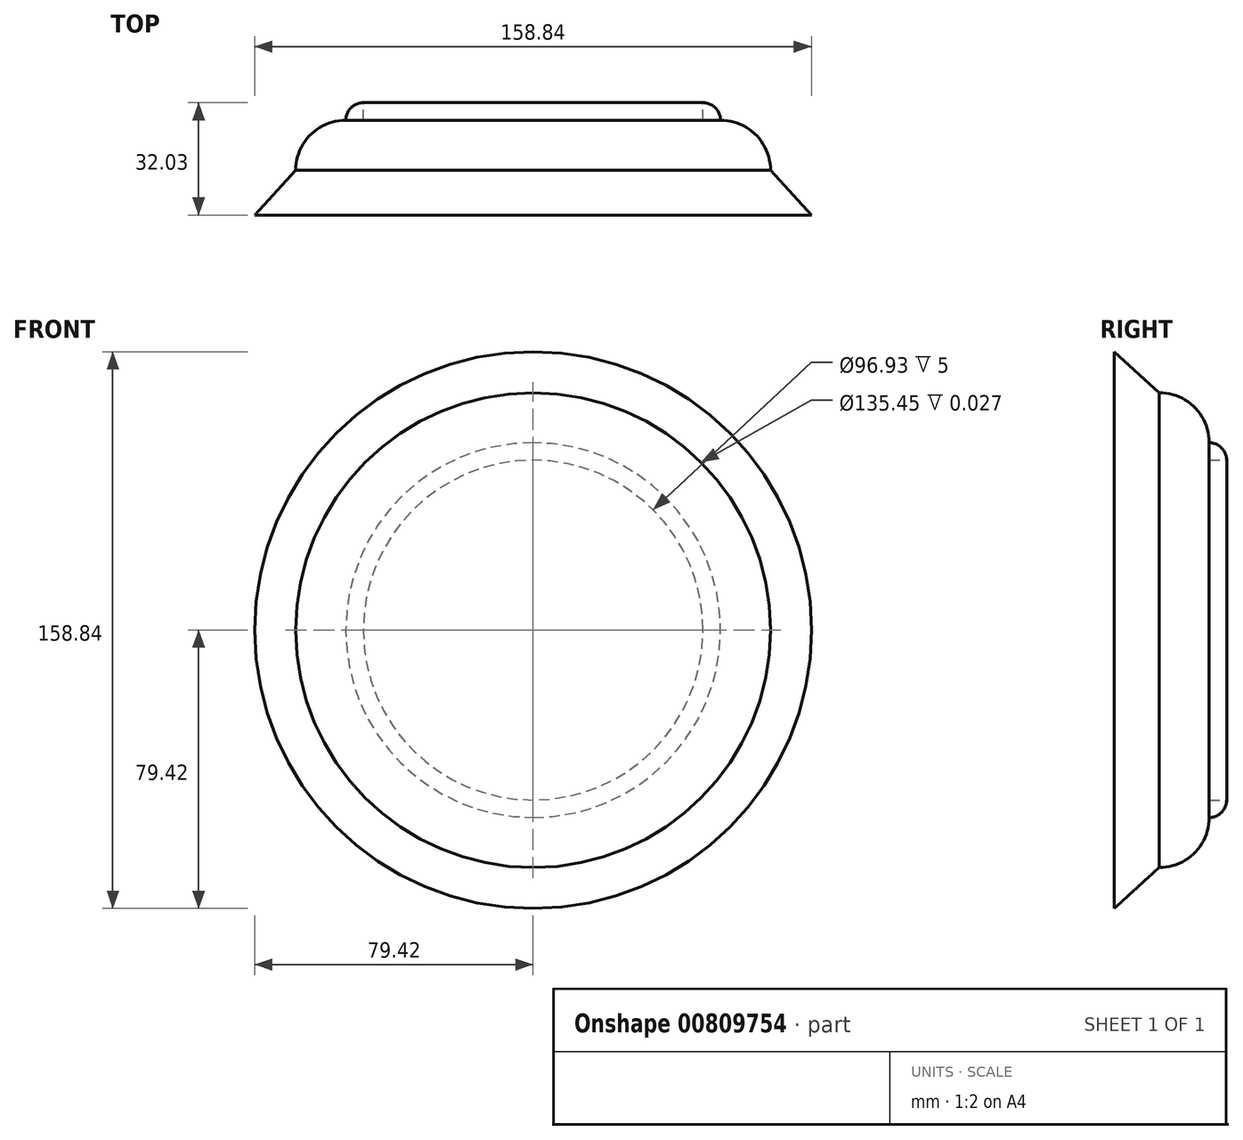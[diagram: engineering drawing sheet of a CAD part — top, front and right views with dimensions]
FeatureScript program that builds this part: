
annotation { "Feature Type Name" : "Feature", "Feature Type Description" : "" }
export const myFeature = defineFeature(function(context is Context, id is Id, definition is map)
    precondition{}
    {
        {
            var Q0;
            Q0=qCreatedBy(makeId("Front.planeOp"),FACE);
            var sketch = newSketch(context, id + "F0", { "sketchPlane" : qUnion([Q0])});
            skCircle(sketch, "E0", {"center": v(0, 0) * mm, "radius": 67.73 * mm});
            skSolve(sketch);
        }
        {
            var Q0;
            Q0=makeQuery(id+"F0.imprint","IMPRINT",FACE,{"disambiguationData":[TD([[makeQuery(id+"F0.imprint","IMPRINT",EDGE,{"derivedFrom":sQuery(id+"F0.wireOp",EDGE,"E0")}),1.0]])]});
            extrude(context, id + "F1", {"entities" : qUnion([Q0]), "depth" : 27 * mm, "offsetDistance" : 25 * mm});
        }
        {
            var Q0;
            Q0=makeQuery(id+"F1.opExtrude","CAP_FACE",FACE,{"disambiguationData":[OSD([sQuery(id+"F0.wireOp",EDGE,"E0")])],"isStart":true});
            var sketch = newSketch(context, id + "F2", { "sketchPlane" : qUnion([Q0])});
            skCircle(sketch, "E1", {"center": v(0, 0) * mm, "radius": 47.7 * mm});
            skSolve(sketch);
        }
        {
            var Q0;
            Q0=makeQuery(id+"F1.opExtrude","CAP_EDGE",EDGE,{"disambiguationData":[OSD([sQuery(id+"F0.wireOp",EDGE,"E0")])],"isStart":true});
            fillet(context, id + "F3", {"entities" : qUnion([Q0]), "radius" : 14.24 * mm, "tangentPropagation" : true, "allowEdgeOverflow" : false});
        }
        {
            var Q0;
            Q0=makeQuery(id+"F2.imprint","IMPRINT",FACE,{"disambiguationData":[TD([[makeQuery(id+"F2.imprint","IMPRINT",EDGE,{"derivedFrom":sQuery(id+"F2.wireOp",EDGE,"E1")}),1.0]])]});
            var sketch = newSketch(context, id + "F4", { "sketchPlane" : qUnion([Q0])});
            skCircle(sketch, "E2", {"center": v(0, 0) * mm, "radius": 53.46 * mm});
            skSolve(sketch);
        }
        {
            var Q0;
            Q0=makeQuery(id+"F4.imprint","IMPRINT",FACE,{"disambiguationData":[TD([[makeQuery(id+"F4.imprint","IMPRINT",EDGE,{"derivedFrom":sQuery(id+"F4.wireOp",EDGE,"E2")}),1.0]])]});
            extrude(context, id + "F5", {"entities" : qUnion([Q0]), "operationType" : NewBodyOperationType.ADD, "depth" : 5 * mm, "offsetDistance" : 25 * mm});
        }
        {
            var Q0;
            Q0=makeQuery(id+"F5.opExtrude","CAP_EDGE",EDGE,{"disambiguationData":[OSD([sQuery(id+"F4.wireOp",EDGE,"E2")])],"isStart":false});
            fillet(context, id + "F6", {"entities" : qUnion([Q0]), "radius" : 5 * mm, "tangentPropagation" : true, "allowEdgeOverflow" : false});
        }
        {
            var Q0;
            Q0=makeQuery(id+"F5.opExtrude","CAP_FACE",FACE,{"disambiguationData":[OSD([sQuery(id+"F2.wireOp",EDGE,"E1"),sQuery(id+"F4.wireOp",EDGE,"E2")])],"isStart":false});
            extrude(context, id + "F7", {"entities" : qUnion([Q0]), "operationType" : NewBodyOperationType.REMOVE, "oppositeDirection" : true, "depth" : 5 * mm, "offsetDistance" : 25 * mm});
        }
        {
            var Q0;
            Q0=qCreatedBy(makeId("Right.planeOp"),FACE);
            var sketch = newSketch(context, id + "F8", { "sketchPlane" : qUnion([Q0])});
            skLineSegment(sketch, "E3", {"start": v(-27.03, 0) * mm, "end": v(0, 0) * mm});
            skLineSegment(sketch, "E4", {"start": v(-27.03, 0) * mm, "end": v(-27.03, 79.42) * mm});
            skLineSegment(sketch, "E5", {"start": v(-27.03, 79.42) * mm, "end": v(-14.24, 67.72) * mm});
            skLineSegment(sketch, "E6", {"start": v(-14.24, 67.72) * mm, "end": v(-27.03, 67.72) * mm});
            skSolve(sketch);
        }
        {
            var Q0;
            Q0=qCreatedBy(makeId("Top.planeOp"),FACE);
            var sketch = newSketch(context, id + "F9", { "sketchPlane" : qUnion([Q0])});
            skLineSegment(sketch, "E7", {"start": v(0, -69.2) * mm, "end": v(0, 69.69) * mm, "construction": true});
            skSolve(sketch);
        }
        {
            var Q0;
            {var subQ0=sQuery(id+"F8.wireOp",EDGE,"E5");Q0=makeQuery(id+"F8.imprint","IMPRINT",FACE,{"disambiguationData":[TD([[makeQuery(id+"F8.imprint","IMPRINT",EDGE,{"derivedFrom":subQ0}),-1.0]])]});}
            var Q1;
            Q1=sQuery(id+"F9.wireOp",EDGE,"E7");
            revolve(context, id + "F10", {"operationType" : NewBodyOperationType.ADD, "surfaceOperationType" : NewSurfaceOperationType.NEW, "entities" : qUnion([Q0]), "axis" : qUnion([Q1]), "revolveType" : RevolveType.FULL});
        }
    });
